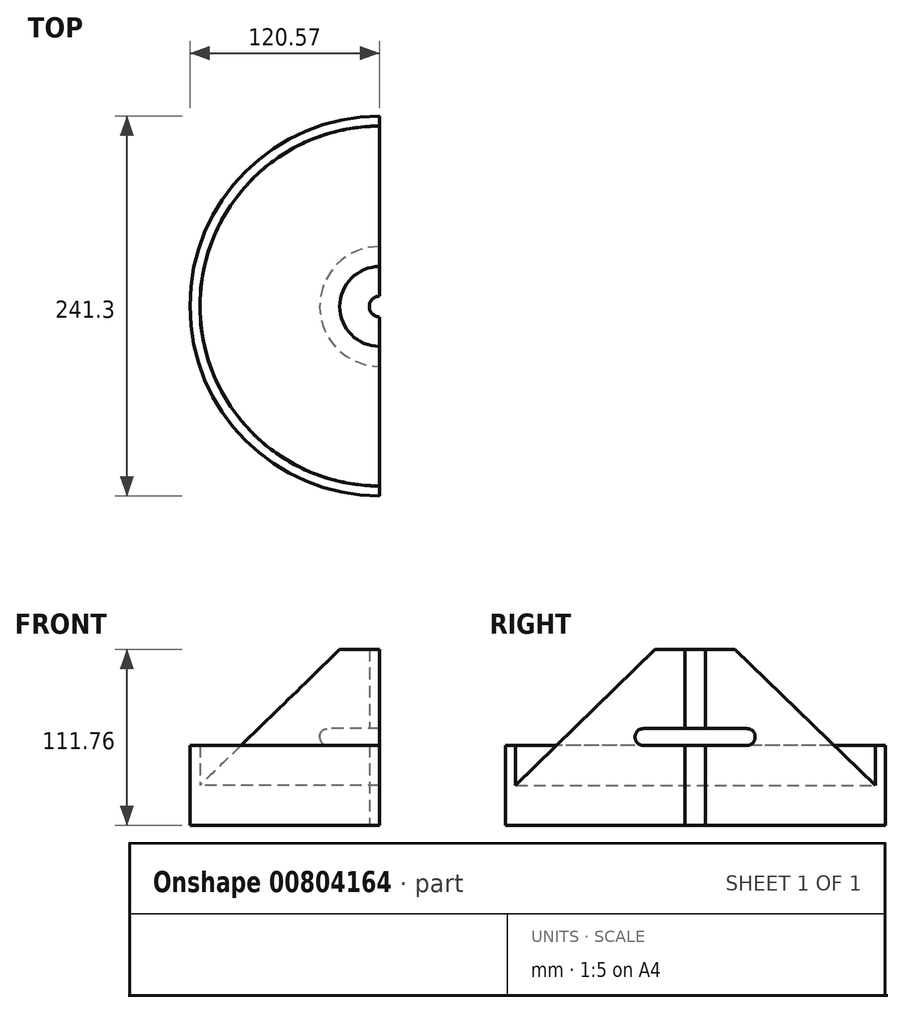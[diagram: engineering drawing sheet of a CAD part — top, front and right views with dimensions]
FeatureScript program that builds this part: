
annotation { "Feature Type Name" : "Feature", "Feature Type Description" : "" }
export const myFeature = defineFeature(function(context is Context, id is Id, definition is map)
    precondition{}
    {
        {
            var Q0;
            Q0=qCreatedBy(makeId("Top.planeOp"),FACE);
            var sketch = newSketch(context, id + "F0", { "sketchPlane" : qUnion([Q0])});
            skArc(sketch, "E0", {"start": v(0, 114.6) * mm, "mid": v(-114.22, 0.3) * mm, "end": v(0, -114) * mm});
            skLineSegment(sketch, "E1", {"start": v(0, 114.6) * mm, "end": v(0, -114) * mm});
            skPoint(sketch, "E2.end.orphan", {"position": v(0, 116) * mm});
            skArc(sketch, "E3.0", {"start": v(0, 120.95) * mm, "mid": v(-120.57, 0.3) * mm, "end": v(0, -120.35) * mm});
            skLineSegment(sketch, "E4", {"start": v(0, 120.95) * mm, "end": v(0, 114.6) * mm});
            skLineSegment(sketch, "E5", {"start": v(0, -114) * mm, "end": v(0, -120.35) * mm});
            skSolve(sketch);
        }
        {
            var Q0;
            Q0=makeQuery(id+"F0.imprint","IMPRINT",FACE,{"disambiguationData":[TD([[makeQuery(id+"F0.imprint","IMPRINT",EDGE,{"derivedFrom":sQuery(id+"F0.wireOp",EDGE,"E0")}),1.0]])]});
            extrude(context, id + "F1", {"entities" : qUnion([Q0]), "depth" : 25.4 * mm, "offsetDistance" : 25.4 * mm});
        }
        {
            var Q0;
            Q0=makeQuery(id+"F0.imprint","IMPRINT",FACE,{"disambiguationData":[TD([[makeQuery(id+"F0.imprint","IMPRINT",EDGE,{"derivedFrom":sQuery(id+"F0.wireOp",EDGE,"E0")}),-1.0]])]});
            extrude(context, id + "F2", {"entities" : qUnion([Q0]), "operationType" : NewBodyOperationType.ADD, "depth" : 50.8 * mm, "offsetDistance" : 25.4 * mm});
        }
        {
            var Q0;
            Q0=qCreatedBy(makeId("Top.planeOp"),FACE);
            cPlane(context, id + "F3", {"entities" : qUnion([Q0]), "cplaneType" : CPlaneType.OFFSET, "offset" : 111.76 * mm, "width" : 152.4 * mm, "height" : 152.4 * mm});
        }
        {
            var Q0;
            Q0=qCreatedBy(id+"F3.planeOp",FACE);
            var sketch = newSketch(context, id + "F4", { "sketchPlane" : qUnion([Q0])});
            skArc(sketch, "E6", {"start": v(0, 25.4) * mm, "mid": v(-25.4, 0) * mm, "end": v(0, -25.4) * mm});
            skLineSegment(sketch, "E7", {"start": v(0, 0) * mm, "end": v(0, 25.4) * mm});
            skLineSegment(sketch, "E8", {"start": v(0, 0) * mm, "end": v(0, -25.4) * mm});
            skSolve(sketch);
        }
        {
            var Q1;
            Q1=makeQuery(id+"F1.opExtrude","CAP_FACE",FACE,{"disambiguationData":[OSD([sQuery(id+"F0.wireOp",EDGE,"E0"),sQuery(id+"F0.wireOp",EDGE,"E1")])],"isStart":false});
            var Q2;
            Q2=makeQuery(id+"F4.imprint","IMPRINT",FACE,{"disambiguationData":[TD([[makeQuery(id+"F4.imprint","IMPRINT",EDGE,{"derivedFrom":sQuery(id+"F4.wireOp",EDGE,"E6")}),1.0]])]});
            var Q3;
            Q3=makeQuery(id+"F1.opExtrude","CAP_VERTEX",VERTEX,{"disambiguationData":[OSD([sQuery(id+"F0.wireOp",EDGE,"E0"),sQuery(id+"F0.wireOp",EDGE,"E1"),sQuery(id+"F0.wireOp",EDGE,"E5")])],"isStart":false});
            var Q4;
            Q4=sQuery(id+"F4.wireOp",VERTEX,"E6.end");
            loft(context, id + "F5", {"operationType" : NewBodyOperationType.ADD, "sheetProfilesArray" : [{ "sheetProfileEntities" : qUnion([Q1]) }, { "sheetProfileEntities" : qUnion([Q2]) }], "matchConnections" : true, "connections" : [{ "connectionEntities" : qUnion([Q3, Q4]), "connectionEdgeQueries" : qUnion([]), "connectionEdgeParameters" : [] }]});
        }
        {
            var Q0;
            Q0=qCreatedBy(makeId("Top.planeOp"),FACE);
            cPlane(context, id + "F6", {"entities" : qUnion([Q0]), "cplaneType" : CPlaneType.OFFSET, "offset" : 25.4 * mm, "width" : 152.4 * mm, "height" : 152.4 * mm});
        }
        {
            var Q0;
            Q0=qCreatedBy(id+"F6.planeOp",FACE);
            cPlane(context, id + "F7", {"entities" : qUnion([Q0]), "cplaneType" : CPlaneType.OFFSET, "offset" : 25.4 * mm, "width" : 152.4 * mm, "height" : 152.4 * mm});
        }
        {
            var Q0;
            Q0=qCreatedBy(id+"F7.planeOp",FACE);
            cPlane(context, id + "F8", {"entities" : qUnion([Q0]), "cplaneType" : CPlaneType.OFFSET, "offset" : 25.4 * mm, "width" : 152.4 * mm, "height" : 152.4 * mm});
        }
        {
            var Q0;
            Q0=qCreatedBy(makeId("Top.planeOp"),FACE);
            var sketch = newSketch(context, id + "F9", { "sketchPlane" : qUnion([Q0])});
            skCircle(sketch, "E9", {"center": v(0, 0) * mm, "radius": 6.6 * mm});
            skSolve(sketch);
        }
        {
            var Q0;
            Q0=makeQuery(id+"F9.imprint","IMPRINT",FACE,{"disambiguationData":[TD([[makeQuery(id+"F9.imprint","IMPRINT",EDGE,{"derivedFrom":sQuery(id+"F9.wireOp",EDGE,"E9")}),1.0]])]});
            extrude(context, id + "F10", {"entities" : qUnion([Q0]), "operationType" : NewBodyOperationType.REMOVE, "depth" : 111.76 * mm, "offsetDistance" : 25.4 * mm});
        }
        {
            var Q0;
            Q0=qCreatedBy(id+"F7.planeOp",FACE);
            var sketch = newSketch(context, id + "F11", { "sketchPlane" : qUnion([Q0])});
            skCircle(sketch, "E10", {"center": v(0, 0) * mm, "radius": 38.1 * mm});
            skSolve(sketch);
        }
        {
            var Q0;
            Q0 = qSketchRegion(id + "F11", true);
            extrude(context, id + "F12", {"entities" : qUnion([Q0]), "operationType" : NewBodyOperationType.REMOVE, "depth" : 10.67 * mm, "offsetDistance" : 25.4 * mm});
        }
        {
            var Q0;
            Q0=makeQuery(id+"F12.boolean.opBoolean","COPY",EDGE,{"derivedFrom":makeQuery(id+"F12.opExtrude","CAP_EDGE",EDGE,{"disambiguationData":[OSD([sQuery(id+"F11.wireOp",EDGE,"E10")])],"isStart":false})});
            var Q1;
            Q1=makeQuery(id+"F12.boolean.opBoolean","COPY",EDGE,{"derivedFrom":makeQuery(id+"F12.opExtrude","CAP_EDGE",EDGE,{"disambiguationData":[OSD([sQuery(id+"F11.wireOp",EDGE,"E10")])],"isStart":true})});
            fillet(context, id + "F13", {"entities" : qUnion([Q0, Q1]), "radius" : 5.08 * mm, "tangentPropagation" : true, "allowEdgeOverflow" : false});
        }
    });
